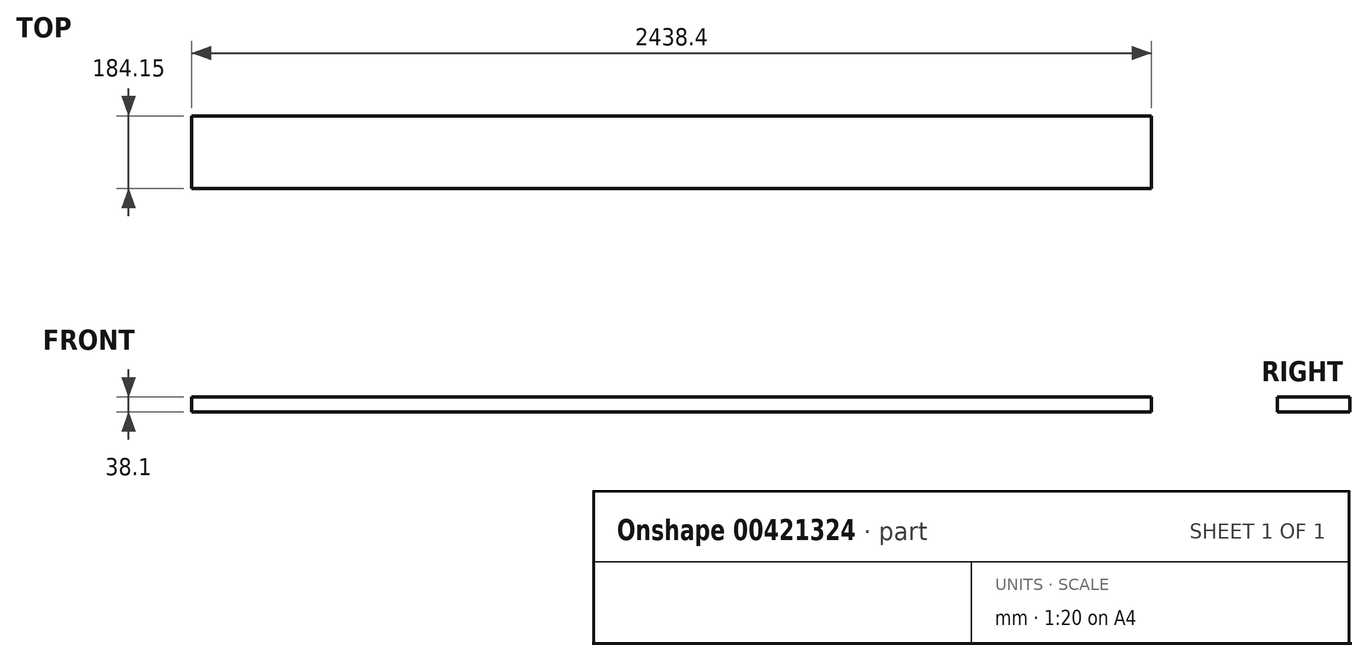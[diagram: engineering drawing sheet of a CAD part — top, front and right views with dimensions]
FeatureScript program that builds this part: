
annotation { "Feature Type Name" : "Feature", "Feature Type Description" : "" }
export const myFeature = defineFeature(function(context is Context, id is Id, definition is map)
    precondition{}
    {
        {
            var Q0;
            Q0=qCreatedBy(makeId("Top.planeOp"),FACE);
            var sketch = newSketch(context, id + "F0", { "sketchPlane" : qUnion([Q0])});
            skLineSegment(sketch, "E0.bottom", {"start": v(-1221.79, -476.64) * mm, "end": v(1216.61, -476.64) * mm});
            skLineSegment(sketch, "E0.top", {"start": v(-1221.79, -292.5) * mm, "end": v(1216.61, -292.5) * mm});
            skLineSegment(sketch, "E0.left", {"start": v(-1221.79, -476.64) * mm, "end": v(-1221.79, -292.5) * mm});
            skLineSegment(sketch, "E0.right", {"start": v(1216.61, -476.64) * mm, "end": v(1216.61, -292.5) * mm});
            skSolve(sketch);
        }
        {
            var Q0;
            Q0=makeQuery(id+"F0.imprint","IMPRINT",FACE,{"disambiguationData":[TD([[makeQuery(id+"F0.imprint","IMPRINT",EDGE,{"derivedFrom":sQuery(id+"F0.wireOp",EDGE,"E0.bottom")}),1.0]])]});
            extrude(context, id + "F1", {"entities" : qUnion([Q0]), "depth" : 38.1 * mm});
        }
    });
